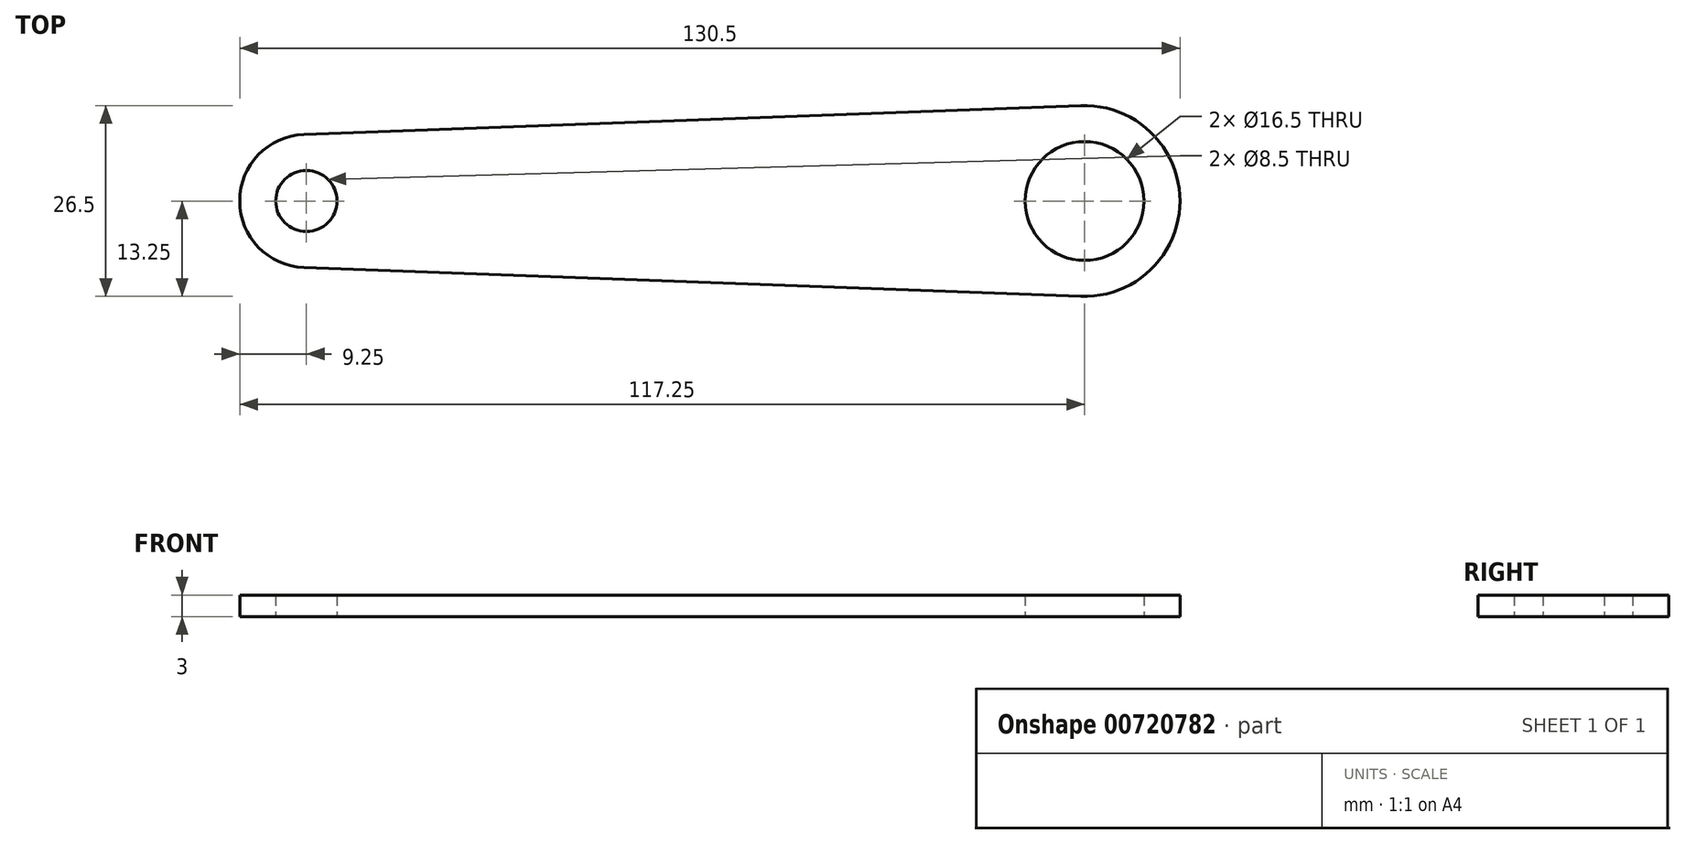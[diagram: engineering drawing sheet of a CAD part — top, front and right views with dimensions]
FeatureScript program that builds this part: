
annotation { "Feature Type Name" : "Feature", "Feature Type Description" : "" }
export const myFeature = defineFeature(function(context is Context, id is Id, definition is map)
    precondition{}
    {
        {
            var Q0;
            Q0=qCreatedBy(makeId("Top.planeOp"),FACE);
            var sketch = newSketch(context, id + "F0", { "sketchPlane" : qUnion([Q0])});
            skCircle(sketch, "E0", {"center": v(0, 0) * mm, "radius": 4.25 * mm});
            skCircle(sketch, "E1", {"center": v(108, 0) * mm, "radius": 8.25 * mm});
            skCircle(sketch, "E2", {"center": v(0, 0) * mm, "radius": 9.25 * mm});
            skCircle(sketch, "E3", {"center": v(108, 0) * mm, "radius": 13.25 * mm});
            skLineSegment(sketch, "E4", {"start": v(-0.34, 9.24) * mm, "end": v(107.5, 13.24) * mm});
            skLineSegment(sketch, "E5", {"start": v(-0.34, -9.24) * mm, "end": v(107.5, -13.24) * mm});
            skLineSegment(sketch, "E6", {"start": v(0, 0) * mm, "end": v(108, 0) * mm, "construction": true});
            skSolve(sketch);
        }
        {
            var Q0;
            {var subQ0=sQuery(id+"F0.wireOp",EDGE,"E4");Q0=makeQuery(id+"F0.imprint","IMPRINT",FACE,{"disambiguationData":[TD([[makeQuery(id+"F0.imprint","IMPRINT",EDGE,{"derivedFrom":subQ0}),-1.0]])]});}
            var Q1;
            Q1=makeQuery(id+"F0.imprint","IMPRINT",FACE,{"disambiguationData":[TD([[makeQuery(id+"F0.imprint","IMPRINT",EDGE,{"derivedFrom":sQuery(id+"F0.wireOp",EDGE,"E0")}),-1.0]])]});
            var Q2;
            Q2=makeQuery(id+"F0.imprint","IMPRINT",FACE,{"disambiguationData":[TD([[makeQuery(id+"F0.imprint","IMPRINT",EDGE,{"derivedFrom":sQuery(id+"F0.wireOp",EDGE,"E1")}),-1.0]])]});
            extrude(context, id + "F1", {"entities" : qUnion([Q0, Q1, Q2]), "depth" : 3 * mm, "offsetDistance" : 25 * mm});
        }
    });
